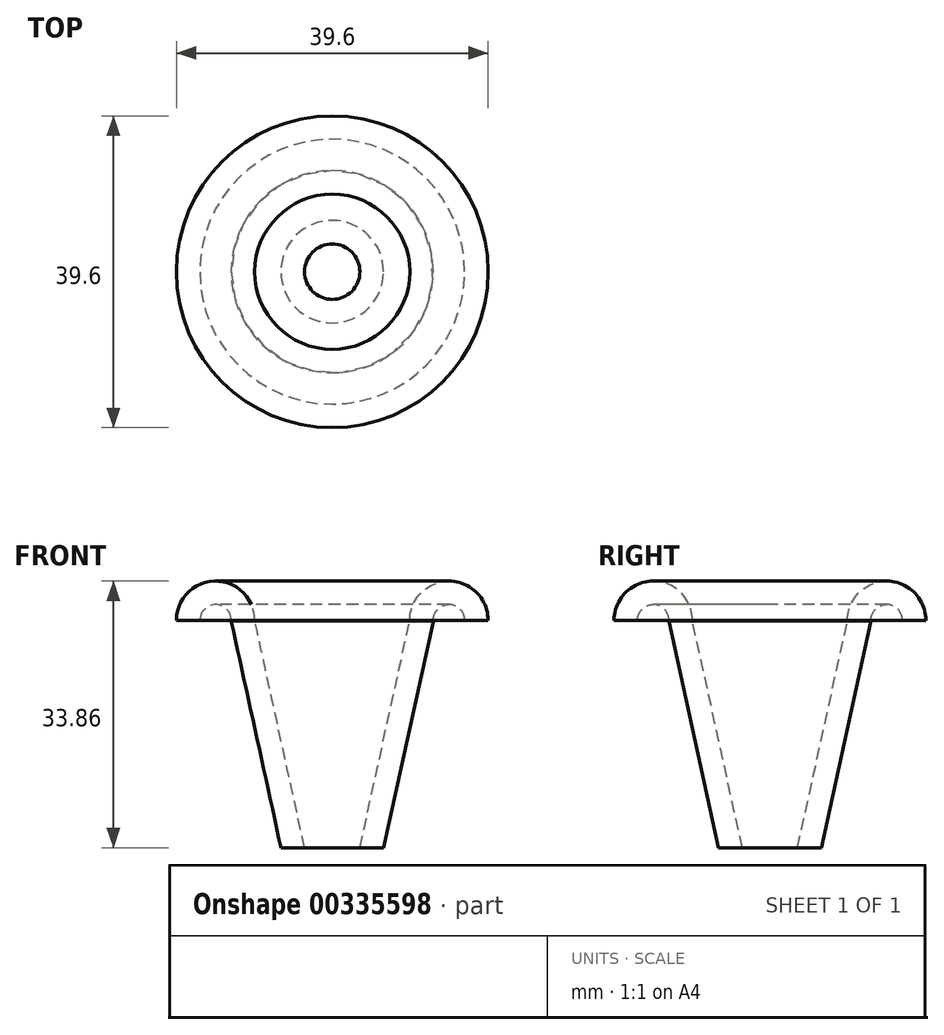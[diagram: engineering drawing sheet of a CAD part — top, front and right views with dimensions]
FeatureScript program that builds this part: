
annotation { "Feature Type Name" : "Feature", "Feature Type Description" : "" }
export const myFeature = defineFeature(function(context is Context, id is Id, definition is map)
    precondition{}
    {
        {
            var Q0;
            Q0=qCreatedBy(makeId("Front.planeOp"),FACE);
            var sketch = newSketch(context, id + "F0", { "sketchPlane" : qUnion([Q0])});
            skArc(sketch, "E0", {"start": v(19.8, 27.46) * mm, "mid": v(14.83, 32.43) * mm, "end": v(9.86, 27.46) * mm});
            skArc(sketch, "E1", {"start": v(16.82, 27.46) * mm, "mid": v(14.77, 29.46) * mm, "end": v(12.83, 27.35) * mm});
            skLineSegment(sketch, "E2", {"start": v(16.82, 27.46) * mm, "end": v(19.8, 27.46) * mm});
            skLineSegment(sketch, "E3", {"start": v(19.8, 27.46) * mm, "end": v(16.82, 27.46) * mm});
            skLineSegment(sketch, "E4", {"start": v(12.83, 27.35) * mm, "end": v(6.51, -1.43) * mm});
            skLineSegment(sketch, "E5", {"start": v(9.86, 27.46) * mm, "end": v(4.84, 4.6) * mm});
            skLineSegment(sketch, "E6", {"start": v(4.84, 4.6) * mm, "end": v(3.51, -1.43) * mm});
            skLineSegment(sketch, "E7", {"start": v(3.51, -1.43) * mm, "end": v(6.51, -1.43) * mm});
            skLineSegment(sketch, "E8", {"start": v(0, 0) * mm, "end": v(0, 9.31) * mm, "construction": true});
            skSolve(sketch);
        }
        {
            var Q0;
            Q0=makeQuery(id+"F0.imprint","IMPRINT",FACE,{"disambiguationData":[TD([[makeQuery(id+"F0.imprint","IMPRINT",EDGE,{"derivedFrom":sQuery(id+"F0.wireOp",EDGE,"E0")}),1.0]])]});
            var Q1;
            Q1=sQuery(id+"F0.wireOp",EDGE,"E8");
            revolve(context, id + "F1", {"entities" : qUnion([Q0]), "axis" : qUnion([Q1]), "revolveType" : RevolveType.FULL});
        }
    });
